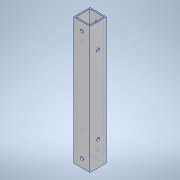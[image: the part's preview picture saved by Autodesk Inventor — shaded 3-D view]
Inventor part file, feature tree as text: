
AUTODESK INVENTOR PART (.ipt)
format: ipt  version: 2020.3 (Build 243373000, 373)  size: 138,752 bytes
history: native  units: mm
features: sketch x4, hole x3, other x1, extrude x1
ambient origin geometry x8: Origin, YZ Plane, XZ Plane, XY Plane, X Axis, Y Axis, Z Axis, Center Point
bodies: Body1 (feature_tree)
feature tree (9):
  other  "ソリッド1"
  extrude  "押し出し1"  Depth=15.0mm
  hole  "穴1"  [1 undecoded]
  hole  "穴2"  [1 undecoded]
  hole  "穴3"  [1 undecoded]
  sketch  "スケッチ1"
  sketch  "スケッチ2"
  sketch  "スケッチ3"
  sketch  "スケッチ4"
note: 3 required parameter values undecoded (feature->parameter linkage not recoverable at this tier; creation-order binding heuristic only, values carry confidence <= 0.55)
